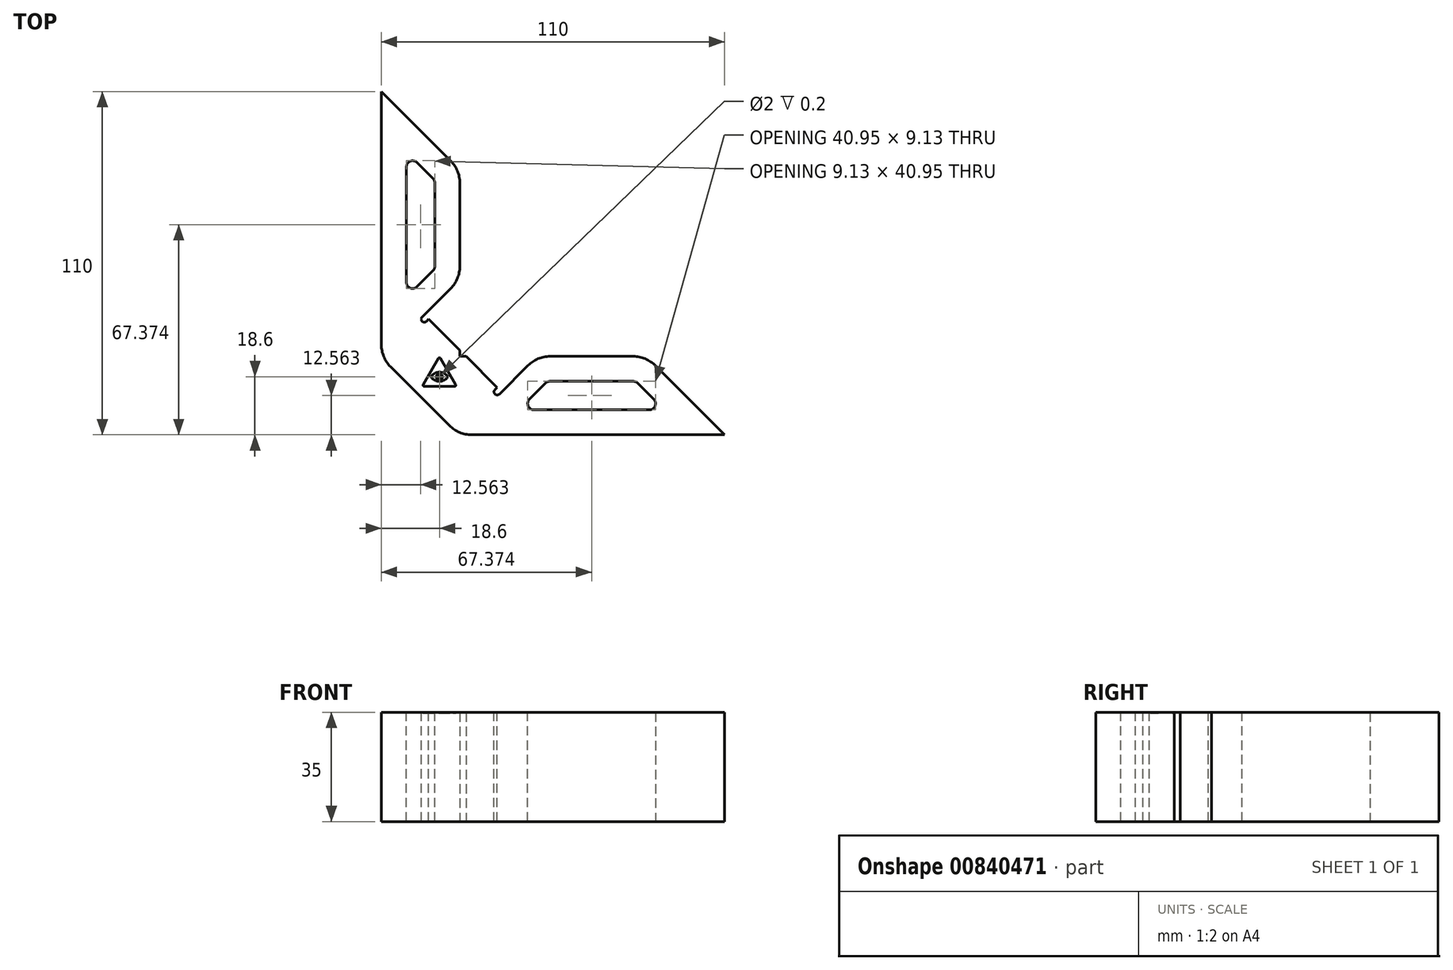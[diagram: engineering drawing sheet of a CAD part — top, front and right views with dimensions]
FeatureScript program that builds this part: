
annotation { "Feature Type Name" : "Feature", "Feature Type Description" : "" }
export const myFeature = defineFeature(function(context is Context, id is Id, definition is map)
    precondition{}
    {
        {
            var Q0;
            Q0=qCreatedBy(makeId("Top.planeOp"),FACE);
            var sketch = newSketch(context, id + "F0", { "sketchPlane" : qUnion([Q0])});
            skLineSegment(sketch, "E0", {"start": v(0, 24.75) * mm, "end": v(0, 110) * mm});
            skLineSegment(sketch, "E1", {"start": v(24.75, 0) * mm, "end": v(110, 0) * mm});
            skLineSegment(sketch, "E2", {"start": v(0, 110) * mm, "end": v(25.13, 84.87) * mm});
            skLineSegment(sketch, "E3", {"start": v(0, 24.75) * mm, "end": v(24.75, 0) * mm});
            skLineSegment(sketch, "E4", {"start": v(13.75, 38.5) * mm, "end": v(25.13, 49.87) * mm});
            skLineSegment(sketch, "E5", {"start": v(25.13, 49.87) * mm, "end": v(25.13, 84.87) * mm});
            skLineSegment(sketch, "E6", {"start": v(0, 0) * mm, "end": v(25.13, 25.13) * mm, "construction": true});
            skLineSegment(sketch, "E7.MirrorCS", {"start": v(110, 0) * mm, "end": v(84.87, 25.13) * mm});
            skLineSegment(sketch, "E8", {"start": v(0, 0) * mm, "end": v(0, 24.75) * mm, "construction": true});
            skLineSegment(sketch, "E9", {"start": v(0, 0) * mm, "end": v(24.75, 0) * mm, "construction": true});
            skLineSegment(sketch, "E10", {"start": v(25.13, 27.13) * mm, "end": v(13.75, 38.5) * mm});
            skLineSegment(sketch, "E11", {"start": v(25.13, 27.13) * mm, "end": v(25.13, 25.13) * mm});
            skPoint(sketch, "E12.orphan", {"position": v(6.52, 31.27) * mm});
            skLineSegment(sketch, "E13.MirrorCS", {"start": v(49.87, 25.13) * mm, "end": v(84.87, 25.13) * mm});
            skLineSegment(sketch, "E14.MirrorCS", {"start": v(38.5, 13.75) * mm, "end": v(49.87, 25.13) * mm});
            skLineSegment(sketch, "E15.MirrorCS", {"start": v(27.13, 25.13) * mm, "end": v(38.5, 13.75) * mm});
            skLineSegment(sketch, "E16.MirrorCS", {"start": v(27.13, 25.13) * mm, "end": v(25.13, 25.13) * mm});
            skLineSegment(sketch, "E17", {"start": v(25.13, 27.13) * mm, "end": v(25.13, 49.87) * mm, "construction": true});
            skSolve(sketch);
        }
        {
            var Q0;
            Q0 = qSketchRegion(id + "F0", true);
            extrude(context, id + "F1", {"entities" : qUnion([Q0]), "depth" : 35 * mm, "offsetDistance" : 25 * mm});
        }
        {
            var Q0;
            Q0=makeQuery(id+"F1.opExtrude","SWEPT_EDGE",EDGE,{"disambiguationData":[OSD([sQuery(id+"F0.wireOp",EDGE,"E7.MirrorCS"),sQuery(id+"F0.wireOp",EDGE,"E13.MirrorCS")])]});
            var Q1;
            Q1=makeQuery(id+"F1.opExtrude","SWEPT_EDGE",EDGE,{"disambiguationData":[OSD([sQuery(id+"F0.wireOp",EDGE,"E4"),sQuery(id+"F0.wireOp",EDGE,"E5")])]});
            var Q2;
            Q2=makeQuery(id+"F1.opExtrude","SWEPT_EDGE",EDGE,{"disambiguationData":[OSD([sQuery(id+"F0.wireOp",EDGE,"E2"),sQuery(id+"F0.wireOp",EDGE,"E5")])]});
            var Q3;
            Q3=makeQuery(id+"F1.opExtrude","SWEPT_EDGE",EDGE,{"disambiguationData":[OSD([sQuery(id+"F0.wireOp",EDGE,"E0"),sQuery(id+"F0.wireOp",EDGE,"E3")])]});
            var Q4;
            Q4=makeQuery(id+"F1.opExtrude","SWEPT_EDGE",EDGE,{"disambiguationData":[OSD([sQuery(id+"F0.wireOp",EDGE,"E1"),sQuery(id+"F0.wireOp",EDGE,"E3")])]});
            var Q5;
            Q5=makeQuery(id+"F1.opExtrude","SWEPT_EDGE",EDGE,{"disambiguationData":[OSD([sQuery(id+"F0.wireOp",EDGE,"E13.MirrorCS"),sQuery(id+"F0.wireOp",EDGE,"E14.MirrorCS")])]});
            fillet(context, id + "F2", {"entities" : qUnion([Q0, Q1, Q2, Q3, Q4, Q5]), "radius" : 10 * mm, "tangentPropagation" : true, "allowEdgeOverflow" : false});
        }
        {
            var Q0;
            Q0=makeQuery(id+"F1.opExtrude","CAP_FACE",FACE,{"disambiguationData":[OSD([sQuery(id+"F0.wireOp",EDGE,"E0"),sQuery(id+"F0.wireOp",EDGE,"E1"),sQuery(id+"F0.wireOp",EDGE,"E2"),sQuery(id+"F0.wireOp",EDGE,"E3"),sQuery(id+"F0.wireOp",EDGE,"79c7Sd2m-oL9w-C5Z7-IeY9-T6gyhu8Q9hIe"),sQuery(id+"F0.wireOp",EDGE,"E4"),sQuery(id+"F0.wireOp",EDGE,"E5"),sQuery(id+"F0.wireOp",EDGE,"adcf64d8-ec03-4bd2-b945-baa081bb2b7b0.MirrorCS"),sQuery(id+"F0.wireOp",EDGE,"E7.MirrorCS"),sQuery(id+"F0.wireOp",EDGE,"adcf64d8-ec03-4bd2-b945-baa081bb2b7b2.MirrorCS"),sQuery(id+"F0.wireOp",EDGE,"adcf64d8-ec03-4bd2-b945-baa081bb2b7b3.MirrorCS")])],"isStart":false});
            var sketch = newSketch(context, id + "F3", { "sketchPlane" : qUnion([Q0])});
            skLineSegment(sketch, "E18", {"start": v(13.75, 38.5) * mm, "end": v(7.85, 32.6) * mm, "construction": true});
            skLineSegment(sketch, "E19", {"start": v(13.75, 38.5) * mm, "end": v(13.04, 37.8) * mm});
            skArc(sketch, "E20", {"start": v(13.04, 37.8) * mm, "mid": v(13.04, 36.38) * mm, "end": v(14.46, 36.38) * mm});
            skLineSegment(sketch, "E21", {"start": v(14.46, 36.38) * mm, "end": v(15.17, 37.09) * mm});
            skLineSegment(sketch, "E22", {"start": v(0, 0) * mm, "end": v(25.13, 25.13) * mm, "construction": true});
            skLineSegment(sketch, "E23.MirrorCS", {"start": v(38.5, 13.75) * mm, "end": v(37.8, 13.04) * mm});
            skLineSegment(sketch, "E24.MirrorCS", {"start": v(36.38, 14.46) * mm, "end": v(37.09, 15.17) * mm});
            skArc(sketch, "E25.MirrorCS", {"start": v(37.8, 13.04) * mm, "mid": v(36.38, 13.04) * mm, "end": v(36.38, 14.46) * mm});
            skLineSegment(sketch, "E26", {"start": v(13.75, 38.5) * mm, "end": v(15.17, 37.09) * mm});
            skLineSegment(sketch, "E27", {"start": v(37.09, 15.17) * mm, "end": v(38.5, 13.75) * mm});
            skSolve(sketch);
        }
        {
            var Q0;
            Q0 = qSketchRegion(id + "F3", true);
            extrude(context, id + "F4", {"entities" : qUnion([Q0]), "operationType" : NewBodyOperationType.REMOVE, "endBound" : BoundingType.THROUGH_ALL, "oppositeDirection" : true, "depth" : 25 * mm, "offsetDistance" : 25 * mm});
        }
        {
            var Q0;
            Q0=makeQuery(id+"F1.opExtrude","CAP_FACE",FACE,{"disambiguationData":[OSD([sQuery(id+"F0.wireOp",EDGE,"E0"),sQuery(id+"F0.wireOp",EDGE,"E1"),sQuery(id+"F0.wireOp",EDGE,"E2"),sQuery(id+"F0.wireOp",EDGE,"E3"),sQuery(id+"F0.wireOp",EDGE,"79c7Sd2m-oL9w-C5Z7-IeY9-T6gyhu8Q9hIe"),sQuery(id+"F0.wireOp",EDGE,"E4"),sQuery(id+"F0.wireOp",EDGE,"E5"),sQuery(id+"F0.wireOp",EDGE,"adcf64d8-ec03-4bd2-b945-baa081bb2b7b0.MirrorCS"),sQuery(id+"F0.wireOp",EDGE,"E7.MirrorCS"),sQuery(id+"F0.wireOp",EDGE,"adcf64d8-ec03-4bd2-b945-baa081bb2b7b2.MirrorCS"),sQuery(id+"F0.wireOp",EDGE,"adcf64d8-ec03-4bd2-b945-baa081bb2b7b3.MirrorCS")])],"isStart":false});
            var sketch = newSketch(context, id + "F5", { "sketchPlane" : qUnion([Q0])});
            skLineSegment(sketch, "E28.0", {"start": v(8, 44.06) * mm, "end": v(16.54, 52.6) * mm});
            skArc(sketch, "E28.1", {"start": v(16.54, 52.6) * mm, "mid": v(16.97, 53.25) * mm, "end": v(17.13, 54.02) * mm});
            skLineSegment(sketch, "E28.2", {"start": v(8, 44.06) * mm, "end": v(8, 90.69) * mm});
            skLineSegment(sketch, "E28.3", {"start": v(8, 90.69) * mm, "end": v(16.54, 82.15) * mm});
            skArc(sketch, "E28.4", {"start": v(17.13, 80.73) * mm, "mid": v(16.97, 81.5) * mm, "end": v(16.54, 82.15) * mm});
            skLineSegment(sketch, "E28.5", {"start": v(17.13, 54.02) * mm, "end": v(17.13, 80.73) * mm});
            skLineSegment(sketch, "E29", {"start": v(0, 0) * mm, "end": v(25.13, 25.13) * mm, "construction": true});
            skPoint(sketch, "E29.endSnap0", {"position": v(0.76, 25.06) * mm});
            skArc(sketch, "E30.MirrorCS", {"start": v(80.73, 17.13) * mm, "mid": v(81.5, 16.97) * mm, "end": v(82.15, 16.54) * mm});
            skArc(sketch, "E31.MirrorCS", {"start": v(52.6, 16.54) * mm, "mid": v(53.25, 16.97) * mm, "end": v(54.02, 17.13) * mm});
            skLineSegment(sketch, "E32.MirrorCS", {"start": v(54.02, 17.13) * mm, "end": v(80.73, 17.13) * mm});
            skLineSegment(sketch, "E33.MirrorCS", {"start": v(44.06, 8) * mm, "end": v(52.6, 16.54) * mm});
            skLineSegment(sketch, "E34.MirrorCS", {"start": v(90.69, 8) * mm, "end": v(82.15, 16.54) * mm});
            skLineSegment(sketch, "E35.MirrorCS", {"start": v(44.06, 8) * mm, "end": v(90.69, 8) * mm});
            skSolve(sketch);
        }
        {
            var Q0;
            Q0 = qSketchRegion(id + "F5", true);
            extrude(context, id + "F6", {"entities" : qUnion([Q0]), "operationType" : NewBodyOperationType.REMOVE, "endBound" : BoundingType.THROUGH_ALL, "oppositeDirection" : true, "depth" : 25 * mm, "offsetDistance" : 25 * mm});
        }
        {
            var Q0;
            Q0=makeQuery(id+"F6.boolean.opBoolean","COPY",EDGE,{"derivedFrom":makeQuery(id+"F6.opExtrude","SWEPT_EDGE",EDGE,{"disambiguationData":[OSD([sQuery(id+"F5.wireOp",EDGE,"E28.2"),sQuery(id+"F5.wireOp",EDGE,"E28.3")])]})});
            var Q1;
            Q1=makeQuery(id+"F6.boolean.opBoolean","COPY",EDGE,{"derivedFrom":makeQuery(id+"F6.opExtrude","SWEPT_EDGE",EDGE,{"disambiguationData":[OSD([sQuery(id+"F5.wireOp",EDGE,"E28.0"),sQuery(id+"F5.wireOp",EDGE,"E28.2")])]})});
            var Q2;
            Q2=makeQuery(id+"F6.boolean.opBoolean","COPY",EDGE,{"derivedFrom":makeQuery(id+"F6.opExtrude","SWEPT_EDGE",EDGE,{"disambiguationData":[OSD([sQuery(id+"F5.wireOp",EDGE,"E33.MirrorCS"),sQuery(id+"F5.wireOp",EDGE,"E35.MirrorCS")])]})});
            var Q3;
            Q3=makeQuery(id+"F6.boolean.opBoolean","COPY",EDGE,{"derivedFrom":makeQuery(id+"F6.opExtrude","SWEPT_EDGE",EDGE,{"disambiguationData":[OSD([sQuery(id+"F5.wireOp",EDGE,"E34.MirrorCS"),sQuery(id+"F5.wireOp",EDGE,"E35.MirrorCS")])]})});
            fillet(context, id + "F7", {"entities" : qUnion([Q0, Q1, Q2, Q3]), "radius" : 2 * mm, "tangentPropagation" : true, "allowEdgeOverflow" : false});
        }
        {
            var Q0;
            Q0=makeQuery(id+"F1.opExtrude","CAP_FACE",FACE,{"disambiguationData":[OSD([sQuery(id+"F0.wireOp",EDGE,"E0"),sQuery(id+"F0.wireOp",EDGE,"E1"),sQuery(id+"F0.wireOp",EDGE,"E2"),sQuery(id+"F0.wireOp",EDGE,"E3"),sQuery(id+"F0.wireOp",EDGE,"E4"),sQuery(id+"F0.wireOp",EDGE,"E5"),sQuery(id+"F0.wireOp",EDGE,"E7.MirrorCS"),sQuery(id+"F0.wireOp",EDGE,"E10"),sQuery(id+"F0.wireOp",EDGE,"E11"),sQuery(id+"F0.wireOp",EDGE,"E13.MirrorCS"),sQuery(id+"F0.wireOp",EDGE,"E14.MirrorCS"),sQuery(id+"F0.wireOp",EDGE,"E15.MirrorCS"),sQuery(id+"F0.wireOp",EDGE,"E16.MirrorCS")])],"isStart":false});
            var sketch = newSketch(context, id + "F8", { "sketchPlane" : qUnion([Q0])});
            skCircle(sketch, "E36", {"center": v(18.6, 18.6) * mm, "radius": 0.5 * mm});
            skCircle(sketch, "E37", {"center": v(18.6, 18.6) * mm, "radius": 1 * mm});
            skLineSegment(sketch, "E38", {"start": v(-22.7, 18.6) * mm, "end": v(59.9, 18.6) * mm, "construction": true});
            skArc(sketch, "E39", {"start": v(21.29, 18.6) * mm, "mid": v(18.6, 20.07) * mm, "end": v(15.91, 18.6) * mm});
            skLineSegment(sketch, "E40.bottom", {"start": v(15.91, 20.07) * mm, "end": v(21.29, 20.07) * mm, "construction": true});
            skLineSegment(sketch, "E40.top", {"start": v(15.91, 17.12) * mm, "end": v(21.29, 17.12) * mm, "construction": true});
            skLineSegment(sketch, "E40.left", {"start": v(15.91, 20.07) * mm, "end": v(15.91, 17.12) * mm, "construction": true});
            skLineSegment(sketch, "E40.right", {"start": v(21.29, 20.07) * mm, "end": v(21.29, 17.12) * mm, "construction": true});
            skLineSegment(sketch, "E41", {"start": v(15.91, 20.07) * mm, "end": v(21.29, 17.12) * mm, "construction": true});
            skLineSegment(sketch, "E42", {"start": v(21.29, 20.07) * mm, "end": v(15.91, 17.12) * mm, "construction": true});
            skArc(sketch, "E43", {"start": v(15.91, 18.6) * mm, "mid": v(18.6, 17.12) * mm, "end": v(21.29, 18.6) * mm});
            skLineSegment(sketch, "E44", {"start": v(18.6, 25.1) * mm, "end": v(18.6, -5.26) * mm, "construction": true});
            skLineSegment(sketch, "E45", {"start": v(18.25, 24.5) * mm, "end": v(13.4, 16.1) * mm});
            skLineSegment(sketch, "E46.MirrorCS", {"start": v(18.95, 24.5) * mm, "end": v(23.8, 16.1) * mm});
            skLineSegment(sketch, "E47", {"start": v(13.75, 15.5) * mm, "end": v(23.45, 15.5) * mm});
            skPoint(sketch, "E48.visualSharp", {"position": v(18.6, 25.1) * mm});
            skArc(sketch, "E48.filletArc", {"start": v(18.95, 24.5) * mm, "mid": v(18.6, 24.7) * mm, "end": v(18.25, 24.5) * mm});
            skPoint(sketch, "E49.visualSharp", {"position": v(24.14, 15.5) * mm});
            skArc(sketch, "E49.filletArc", {"start": v(23.45, 15.5) * mm, "mid": v(23.8, 15.7) * mm, "end": v(23.8, 16.1) * mm});
            skPoint(sketch, "E50.visualSharp", {"position": v(13.06, 15.5) * mm});
            skArc(sketch, "E50.filletArc", {"start": v(13.4, 16.1) * mm, "mid": v(13.4, 15.7) * mm, "end": v(13.75, 15.5) * mm});
            skLineSegment(sketch, "E51", {"start": v(0, 0) * mm, "end": v(25.13, 25.13) * mm, "construction": true});
            skSolve(sketch);
        }
        {
            var Q0;
            Q0 = qSketchRegion(id + "F8", true);
            extrude(context, id + "F9", {"entities" : qUnion([Q0]), "operationType" : NewBodyOperationType.REMOVE, "oppositeDirection" : true, "depth" : 0.2 * mm, "offsetDistance" : 25 * mm});
        }
        {
            var Q0;
            {var subQ2=sQuery(id+"F0.wireOp",EDGE,"E16.MirrorCS");var subQ3=sQuery(id+"F0.wireOp",EDGE,"E15.MirrorCS");var subQ4=sQuery(id+"F0.wireOp",EDGE,"E14.MirrorCS");var subQ5=sQuery(id+"F0.wireOp",EDGE,"E13.MirrorCS");var subQ6=sQuery(id+"F0.wireOp",EDGE,"E11");var subQ7=sQuery(id+"F0.wireOp",EDGE,"E10");var subQ8=sQuery(id+"F0.wireOp",EDGE,"E7.MirrorCS");var subQ9=sQuery(id+"F0.wireOp",EDGE,"E5");var subQ10=sQuery(id+"F0.wireOp",EDGE,"E4");var subQ11=sQuery(id+"F0.wireOp",EDGE,"E3");var subQ12=sQuery(id+"F0.wireOp",EDGE,"E2");var subQ13=sQuery(id+"F0.wireOp",EDGE,"E1");var subQ14=sQuery(id+"F0.wireOp",EDGE,"E0");Q0=makeQuery(id+"F9.boolean.opBoolean","SPLIT",FACE,{"disambiguationData":[TD([makeQuery(id+"F1.opExtrude","SWEPT_FACE",FACE,{"disambiguationData":[OSD([subQ14])]})])],"derivedFrom":makeQuery(id+"F1.opExtrude","CAP_FACE",FACE,{"disambiguationData":[OSD([subQ14,subQ13,subQ12,subQ11,subQ10,subQ9,subQ8,subQ7,subQ6,subQ5,subQ4,subQ3,subQ2])],"isStart":false})});}
            var sketch = newSketch(context, id + "F10", { "sketchPlane" : qUnion([Q0])});
            skCircle(sketch, "E52.0", {"center": v(18.6, 18.6) * mm, "radius": 1 * mm});
            skCircle(sketch, "E52.1", {"center": v(18.6, 18.6) * mm, "radius": 0.5 * mm});
            skSolve(sketch);
        }
        {
            var Q0;
            Q0 = qSketchRegion(id + "F10", true);
            var Q1;
            Q1=makeQuery(id+"F9.boolean.opBoolean","COPY",FACE,{"derivedFrom":makeQuery(id+"F9.opExtrude","CAP_FACE",FACE,{"disambiguationData":[OSD([sQuery(id+"F8.wireOp",EDGE,"E39"),sQuery(id+"F8.wireOp",EDGE,"E43"),sQuery(id+"F8.wireOp",EDGE,"E45"),sQuery(id+"F8.wireOp",EDGE,"E46.MirrorCS"),sQuery(id+"F8.wireOp",EDGE,"E47"),sQuery(id+"F8.wireOp",EDGE,"E48.filletArc"),sQuery(id+"F8.wireOp",EDGE,"E49.filletArc"),sQuery(id+"F8.wireOp",EDGE,"E50.filletArc")])],"isStart":false})});
            extrude(context, id + "F11", {"entities" : qUnion([Q0]), "operationType" : NewBodyOperationType.REMOVE, "endBound" : BoundingType.UP_TO_SURFACE, "oppositeDirection" : true, "depth" : 0.2 * mm, "endBoundEntityFace" : qUnion([Q1]), "offsetDistance" : 25 * mm});
        }
    });
